# Revit family: PRD_FrankeWS_Splshbcks_SiriusSplashback_F831
name_source: partatom
category: Furniture
revit_build: Autodesk Revit 2018 (Build: 20190510_1515(x64)
units: mm (PartAtom-declared; Revit-internal decimal feet)

## family parameters
Cut with Voids When Loaded = No
Host = Face
OmniClass Number = 23.45.00.00
OmniClass Title = Sanitary, Laundry, and Cleaning Equipment
Room Calculation Point = No
Shared = No

## types (1)
- F831
    AssetType = Fixed
    BIMObjectName = PRD_AR_Splashbacks_SiriusSplashback_F831
    Category = Pr_40_20_76_83, Splashbacks
    Color = Stainless steel
    Default Elevation = 850 mm  [stored 2.78871 ft]
    Description = Splash back for fixing onto general purpose sink type WB500GV, stainless steel, surface satin finished, material thickness, 0.9 mm, incl. mounting set.
    DurationUnit = year
    Edges = Square
    Features = stainless steel, 0.90 mm, satin finished, wall mounting, 500x250x4 mm (WxHxD)
    Finish = Satin finished
    GrossWeight = 1.50 kg
    IfcExportAs = IfcFurnitureType
    IfcExportType = NOTDEFINED
    MainColor = Stainless steel
    Manufacturer = KWC Group AG
    ManufacturerName = KWC Group AG
    ManufacturerURL = www.kwc.com
    Material = Stainless steel 1.4301
    Model = F831
    ModelNumber = 2000057029
    ModelReference = F831
    NBSDescription = Splashbacks
    NBSReference = 45-35-15/464
    Name = Sirius splashback F831
    NetWeight = 1.10 kg
    NominalDepth = 4 mm  [stored 0.0131234 ft]
    NominalHeight = 250 mm  [stored 0.82021 ft]
    NominalLength = 500 mm  [stored 1.64042 ft]
    NominalWidth = 0 mm  [stored 0 ft]
    ProductInformation = https://pim.kwc.com
    Shape = Rectangular
    Size = 500 x 250 x 4 mm
    SplashbackMaterial = PRD_AR_StainlessSteel_SatinFinished
    Style = Splashback
    URL = www.kwc.com
    Uniclass2015Code = Pr_40_20_76_83
    Uniclass2015Title = Splashbacks
    Uniclass2015Version = Products v1.5
    Version = 1
    WarrantyDurationUnit = year

note: [stored X ft] marks values corroborated as IEEE doubles in the binary element streams (Revit-internal decimal feet)

## geometry (parser evidence)
native form markers: Sweep x3
no freeform markers — native parametric forms only
